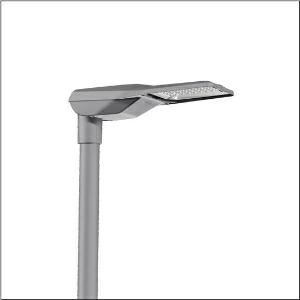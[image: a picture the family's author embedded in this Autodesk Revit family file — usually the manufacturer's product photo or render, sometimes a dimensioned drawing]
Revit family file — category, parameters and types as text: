
# Revit family: streetlight_sl_21_iq_mini___st1_5a_5xe2p31d08hb_3c75
name_source: partatom
category: Lighting Fixtures
units: mm (PartAtom-declared; Revit-internal decimal feet)

## family parameters
Cut with Voids When Loaded = No
Host = Face
Light Source = No
Part Type = Normal
Room Calculation Point = No
Round Connector Dimension = Use Diameter
Shared = No

## types (1)
- --- (1 x LED, 9290 lm, 70.9 W, 3000K)
    Apparent Load = 71 VA
    CIE Flux Codes = 22 53 95 100 100
    Color Rendering = 70
    Color Temperature = 3000K
    Default Elevation = 1800 mm
    Description = Streetlight SL 21 iQ mini, mast luminaire, primary light control with lens, of PMMA, primary optical cover: cover, of toughened safety glass, transparent, light distribution: ST1.5a, light emission: direct distribution, primary light characteristic: asymmetric, installation type: post-top, side-entry, LED, High Power LED, rated luminous flux: 9.290lm, luminous efficacy: 131lm/W, light colour: 730, colour temperature: 3000K, control: Auto-Match, Temp-Guard, Lumen-Switch, Night-Set, Smart-Wire, Light-Fading, Desk-Remote (wireless, voltage-free reading and setting of iQ features in the workshop via application-optimized NFC function/RFID function), optimised constant luminous flux control (CLO 2.0), presetting dimming linear, mains connection: 220..240V, AC, 50/60Hz, start of lifetime: 71W, end of service life: 75W, reduction: 31W, luminaire housing, of diecast aluminium, powder-coated, Siteco® metallic grey (DB 702S), corrosivity category C5 mid according to DIN EN ISO 12944, please order mast flange separately, inclination adjustable: 0°, 5°, 10°, 15°, sealing non-destructively replaceable, multi-level sealing system, length: 628mm, width: 235mm, height: 110mm, mast flange for spigot size: 42mm (side-entry): 5XC10008XM4, 60/48mm (side-entry/post-top): 5XC10108XM2, 76/60mm (side-entry/post-top): 5XC10108XM1, protection rating (complete): IP66, insulation class (complete): insulation class II (safety insulation), certification: CE, ENEC, ENEC+, VDE, impact resistance: IK09, permissible operating ambient temperature for outdoor applications: -40..+50°C, standard-compliant lighting for roads and squares, packaging unit: 1 piece

Light Distribution: ST1.5a
    Height = 110 mm
    Lamp = 1 x LED
    Lamp Light Flux = 9290 lm
    Lamp Power = 70.9 W
    Lamp count = 1
    Length = 625 mm
    Luminous efficacy = 131 lm/W
    Manufacturer = Siteco
    ModVariant = No
    Model = 5XE2P31D08HB
    Number of Poles = 1
    OnlyDefault = Yes
    Power Factor = 1
    Product Name = Streetlight SL 21 iQ mini | ST1.5a
    Product group = mast luminaire | pylon top
    ProductGroupID = 6100
    Protection Class = Protection class II
    Protection Degree = IP 66
    RLX_Detail_Level = 1
    RLX_Emergency_Light_Flux = 0 lm
    RLX_Emergency_Type = 0
    RLX_Emergency_Type_DB = No
    RlxData = <blob elided: 95953 chars, md5=791dae16>
    Socket = socket
    Standby Power = 0 W
    System Light Flux = 9290 lm
    System Power = 71 W
    Type Comments = factory setting: luminous flux: 100 % | dim-lin: 254 | 711 mA
    Type Image = l_1003519.jpg
    URL = http://relux.com
    VarID = @adj_107283
    Voltage = 0 V
    Weight = 0.00 kg
    Width = 234 mm

## geometry (parser evidence)
native form markers: Blend x4, Sweep x9
no freeform markers — native parametric forms only
